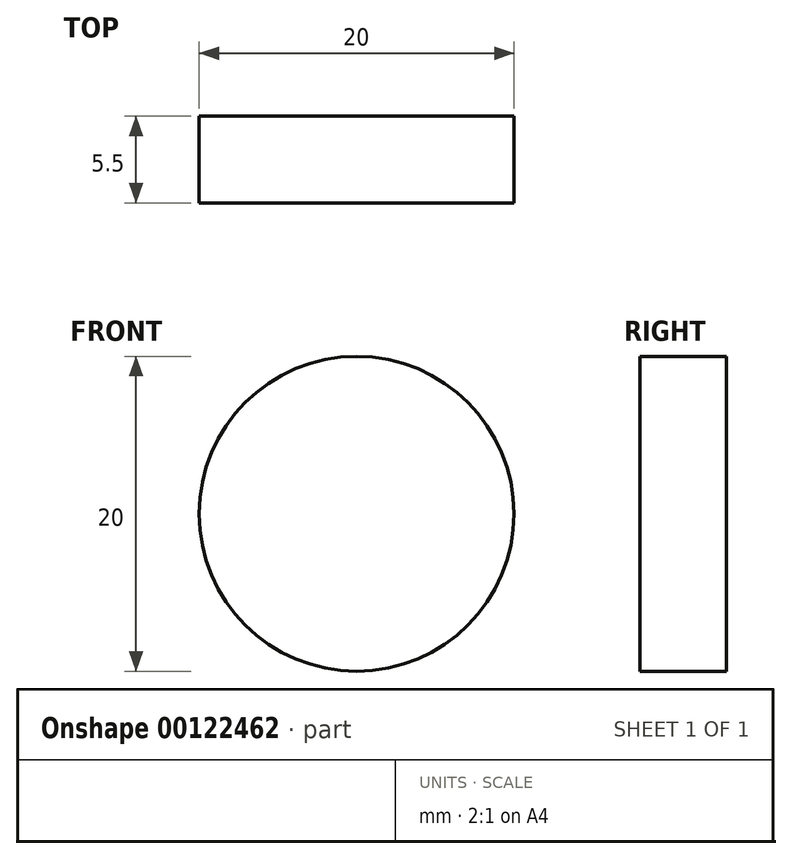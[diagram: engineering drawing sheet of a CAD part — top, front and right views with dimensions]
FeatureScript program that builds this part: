
annotation { "Feature Type Name" : "Feature", "Feature Type Description" : "" }
export const myFeature = defineFeature(function(context is Context, id is Id, definition is map)
    precondition{}
    {
        {
            var Q0;
            Q0=qCreatedBy(makeId("Front.planeOp"),FACE);
            var sketch = newSketch(context, id + "F0", { "sketchPlane" : qUnion([Q0])});
            skCircle(sketch, "E0", {"center": v(0, 0) * mm, "radius": 10 * mm});
            skSolve(sketch);
        }
        {
            var Q0;
            Q0 = qSketchRegion(id + "F0", true);
            extrude(context, id + "F1", {"entities" : qUnion([Q0]), "depth" : 5.5 * mm, "offsetDistance" : 25 * mm});
        }
    });
